# Revit family: Accessory-Towel_Bar-KOHLER-STILLNESS-K-14451T
name_source: partatom
category: Specialty Equipment
revit_build: Autodesk Revit 2017 (Build: 20160225_1515(x64)
units: mm (PartAtom-declared; Revit-internal decimal feet)

## family parameters
Cut with Voids When Loaded = No
Host = Face
OmniClass Number = 23.31.25.25
OmniClass Title = Towel Bars
Part Type = Normal
Room Calculation Point = No
Round Connector Dimension = Use Diameter
Shared = No

## types (5) — shared parameters
ADA Compliant = No
Assembly Code = C1030200
Date Modified = 06/08/2020
Default Elevation = 42"
Description = 24 inch Towel Bar
Height = 1 7/8"
Length = 3 3/16"
Manufacturer = KOHLER Co.
Master Format 2014 = 10 28 00
Master Format 2014 Name = Toilet, Bath, and Laundry Accessories
Material = Solid Brass Construction
Product Documentation Link = http://files.kohler.com.cn
Product Name = STILLNESS
Product Page URL = http://www.kohler.com.cn
URL = http://www.kohler.com.cn
WaterSense Certified = No
Width = 24"

## per-type parameters (varying)
| type | Finish | Model | Type |
| CP-Polished Chrome | Kohler-Metal-CP-Polished_Chrome | K-14451T-CP | 1 |
| BN-Roman Silver | Kohler-Metal-BN-Roman_Silver | K-14451T-BN | 2 |
| PGD-Eternal Gold | Kohler-Metal-PGD-Eternal_Gold | K-14451T-PGD | 3 |
| RGD-Rose Gold | Kohler-Metal-RGD-Rose_Gold | K-14451T-RGD | 4 |
| SN-Champagne Gold | Kohler-Metal-SN-Champagne_Gold | K-14451T-SN | 5 |

## geometry (parser evidence)
native form markers: Sweep x6
no freeform markers — native parametric forms only
